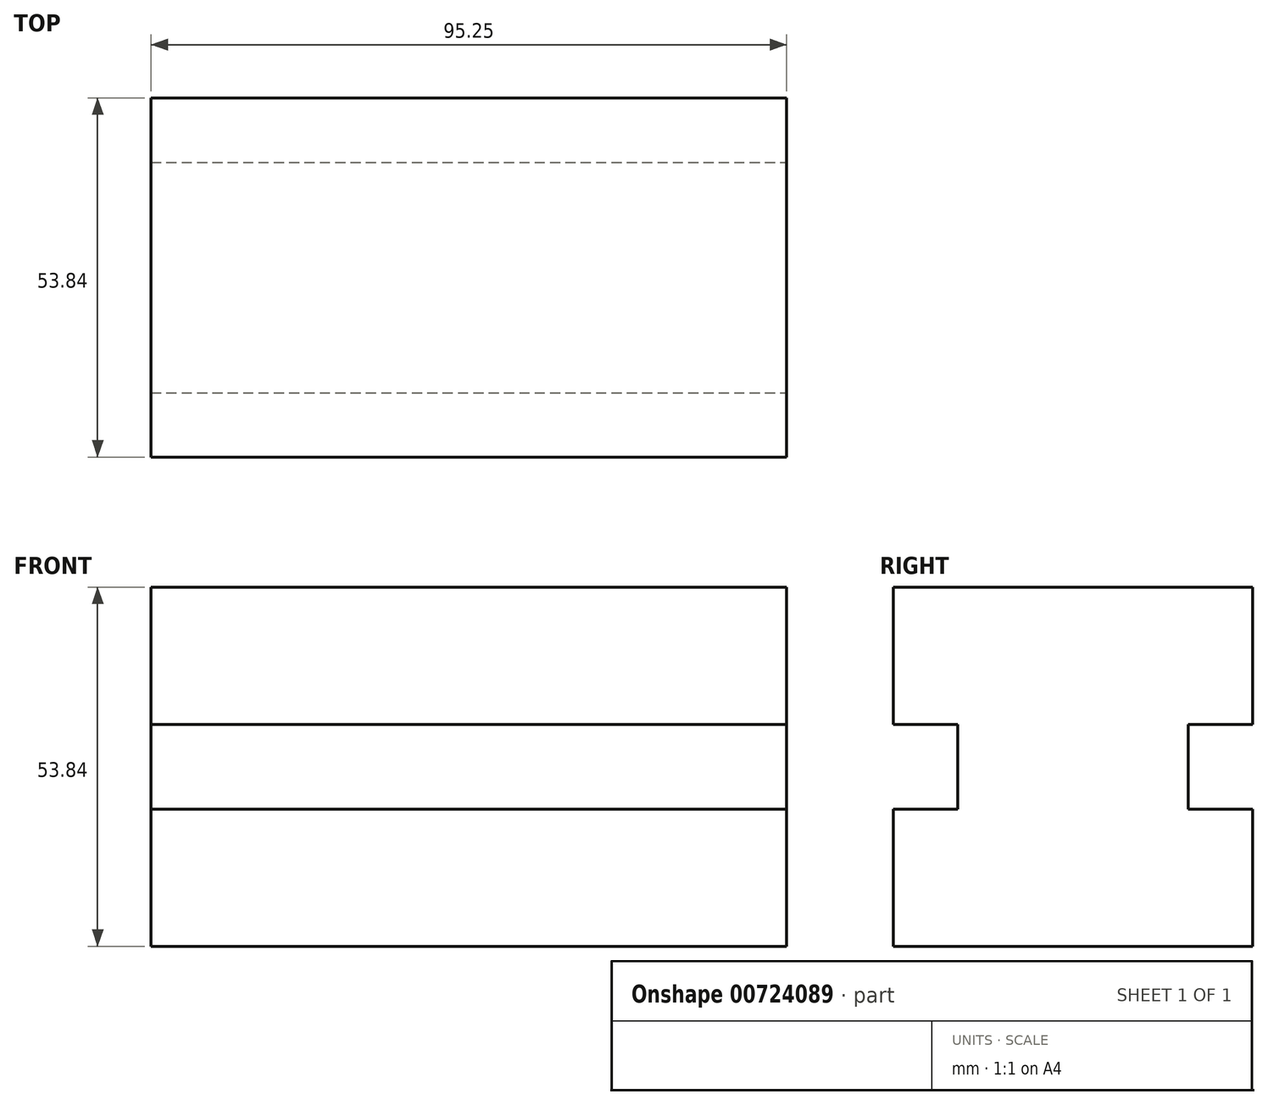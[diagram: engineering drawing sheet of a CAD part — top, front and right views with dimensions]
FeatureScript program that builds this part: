
annotation { "Feature Type Name" : "Feature", "Feature Type Description" : "" }
export const myFeature = defineFeature(function(context is Context, id is Id, definition is map)
    precondition{}
    {
        {
            var Q0;
            Q0=qCreatedBy(makeId("Right.planeOp"),FACE);
            var sketch = newSketch(context, id + "F0", { "sketchPlane" : qUnion([Q0])});
            skLineSegment(sketch, "E0.bottom", {"start": v(26.92, -26.92) * mm, "end": v(-26.92, -26.92) * mm});
            skLineSegment(sketch, "E0.top", {"start": v(26.92, 26.92) * mm, "end": v(-26.92, 26.92) * mm});
            skLineSegment(sketch, "E0.left", {"start": v(26.92, -26.92) * mm, "end": v(26.92, -6.35) * mm});
            skLineSegment(sketch, "E0.right", {"start": v(-26.92, -26.92) * mm, "end": v(-26.92, -6.35) * mm});
            skPoint(sketch, "E0.middle", {"position": v(0, 0) * mm});
            skLineSegment(sketch, "E1.bottom", {"start": v(-26.92, 6.35) * mm, "end": v(-17.27, 6.35) * mm});
            skLineSegment(sketch, "E1.top", {"start": v(-26.92, -6.35) * mm, "end": v(-17.27, -6.35) * mm});
            skLineSegment(sketch, "E1.right", {"start": v(-17.27, 6.35) * mm, "end": v(-17.27, -6.35) * mm});
            skLineSegment(sketch, "E2.trimOffspring", {"start": v(-26.92, 6.35) * mm, "end": v(-26.92, 26.92) * mm});
            skLineSegment(sketch, "E3", {"start": v(0, 31.9) * mm, "end": v(0, -28.47) * mm, "construction": true});
            skPoint(sketch, "E3.startSnap0", {"position": v(0, 26.92) * mm});
            skLineSegment(sketch, "E4.MirrorCS", {"start": v(26.92, 6.35) * mm, "end": v(17.27, 6.35) * mm});
            skLineSegment(sketch, "E5.MirrorCS", {"start": v(17.27, 6.35) * mm, "end": v(17.27, -6.35) * mm});
            skLineSegment(sketch, "E6.MirrorCS", {"start": v(26.92, -6.35) * mm, "end": v(17.27, -6.35) * mm});
            skLineSegment(sketch, "E7.trimOffspring", {"start": v(26.92, 6.35) * mm, "end": v(26.92, 26.92) * mm});
            skSolve(sketch);
        }
        {
            var Q0;
            Q0=makeQuery(id+"F0.imprint","IMPRINT",FACE,{"disambiguationData":[TD([[makeQuery(id+"F0.imprint","IMPRINT",EDGE,{"derivedFrom":sQuery(id+"F0.wireOp",EDGE,"E0.bottom")}),-1.0]])]});
            extrude(context, id + "F1", {"entities" : qUnion([Q0]), "oppositeDirection" : true, "depth" : 95.25 * mm, "offsetDistance" : 25.4 * mm});
        }
    });
